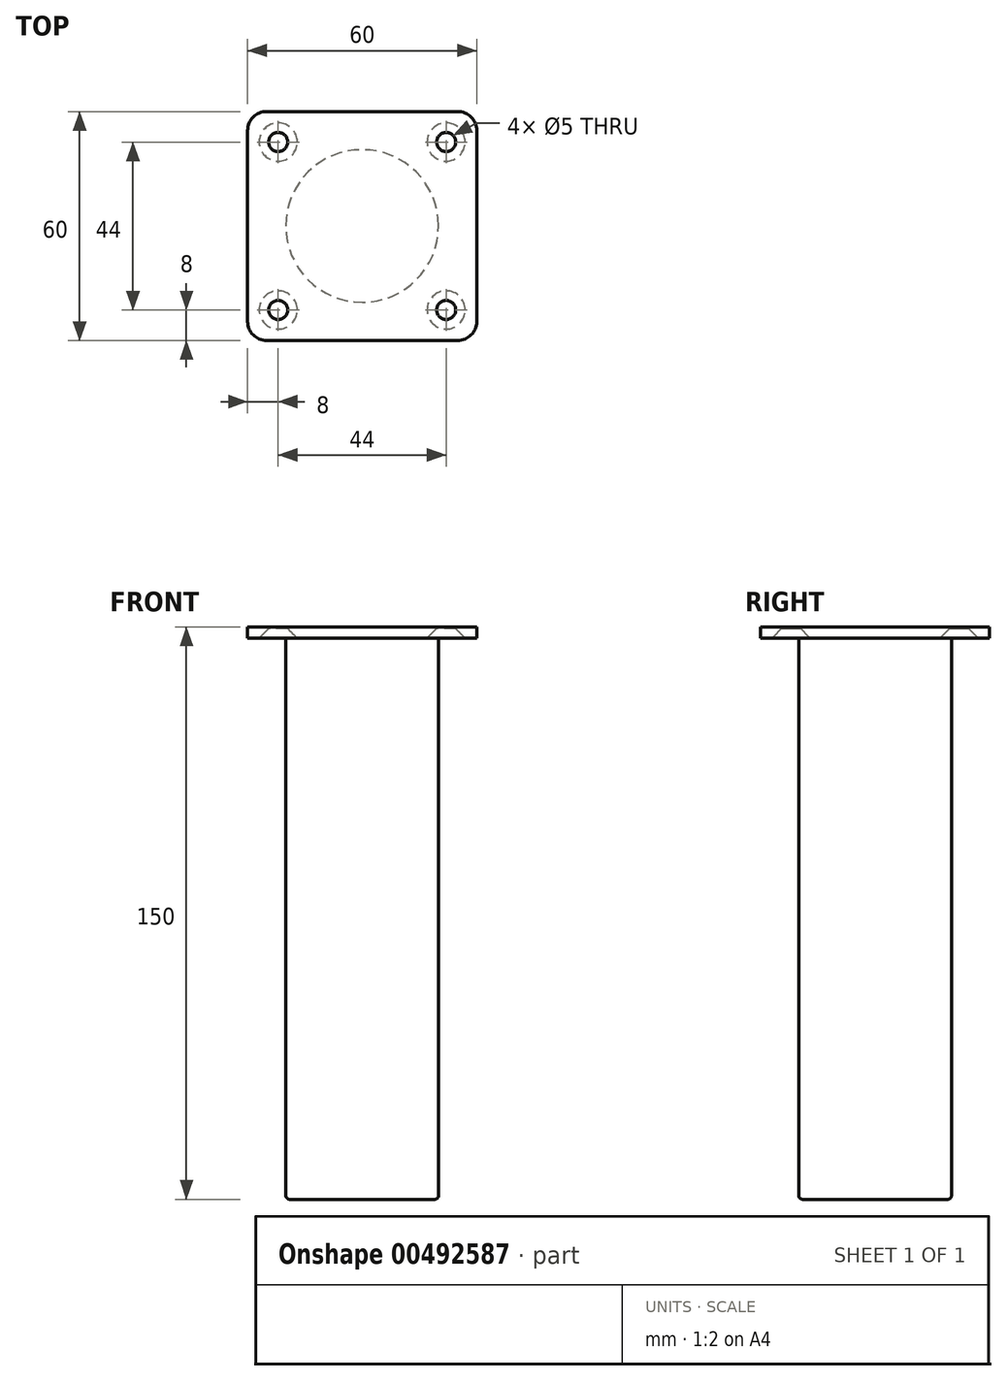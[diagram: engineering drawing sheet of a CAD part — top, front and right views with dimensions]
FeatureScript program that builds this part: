
annotation { "Feature Type Name" : "Feature", "Feature Type Description" : "" }
export const myFeature = defineFeature(function(context is Context, id is Id, definition is map)
    precondition{}
    {
        {
            var Q0;
            Q0=qCreatedBy(makeId("Top.planeOp"),FACE);
            var sketch = newSketch(context, id + "F0", { "sketchPlane" : qUnion([Q0])});
            skLineSegment(sketch, "E0.bottom", {"start": v(-30, 30) * mm, "end": v(30, 30) * mm});
            skLineSegment(sketch, "E0.top", {"start": v(-30, -30) * mm, "end": v(30, -30) * mm});
            skLineSegment(sketch, "E0.left", {"start": v(-30, 30) * mm, "end": v(-30, -30) * mm});
            skLineSegment(sketch, "E0.right", {"start": v(30, 30) * mm, "end": v(30, -30) * mm});
            skPoint(sketch, "E0.middle", {"position": v(0, 0) * mm});
            skSolve(sketch);
        }
        {
            var Q0;
            Q0=makeQuery(id+"F0.imprint","IMPRINT",FACE,{"disambiguationData":[TD([[makeQuery(id+"F0.imprint","IMPRINT",EDGE,{"derivedFrom":sQuery(id+"F0.wireOp",EDGE,"E0.bottom")}),-1.0]])]});
            extrude(context, id + "F1", {"entities" : qUnion([Q0]), "oppositeDirection" : true, "depth" : 3 * mm});
        }
        {
            var Q0;
            Q0=makeQuery(id+"F1.opExtrude","CAP_FACE",FACE,{"disambiguationData":[OSD([sQuery(id+"F0.wireOp",EDGE,"E0.bottom"),sQuery(id+"F0.wireOp",EDGE,"E0.top"),sQuery(id+"F0.wireOp",EDGE,"E0.left"),sQuery(id+"F0.wireOp",EDGE,"E0.right")])],"isStart":false});
            var sketch = newSketch(context, id + "F2", { "sketchPlane" : qUnion([Q0])});
            skCircle(sketch, "E1", {"center": v(0, 0) * mm, "radius": 20 * mm});
            skSolve(sketch);
        }
        {
            var Q0;
            Q0 = qSketchRegion(id + "F2", true);
            extrude(context, id + "F3", {"entities" : qUnion([Q0]), "operationType" : NewBodyOperationType.ADD, "depth" : 147 * mm});
        }
        {
            var Q0;
            Q0=makeQuery(id+"F1.opExtrude","SWEPT_EDGE",EDGE,{"disambiguationData":[OSD([sQuery(id+"F0.wireOp",EDGE,"E0.top"),sQuery(id+"F0.wireOp",EDGE,"E0.left")])]});
            var Q1;
            Q1=makeQuery(id+"F1.opExtrude","SWEPT_EDGE",EDGE,{"disambiguationData":[OSD([sQuery(id+"F0.wireOp",EDGE,"E0.top"),sQuery(id+"F0.wireOp",EDGE,"E0.right")])]});
            var Q2;
            Q2=makeQuery(id+"F1.opExtrude","SWEPT_EDGE",EDGE,{"disambiguationData":[OSD([sQuery(id+"F0.wireOp",EDGE,"E0.bottom"),sQuery(id+"F0.wireOp",EDGE,"E0.right")])]});
            var Q3;
            Q3=makeQuery(id+"F1.opExtrude","SWEPT_EDGE",EDGE,{"disambiguationData":[OSD([sQuery(id+"F0.wireOp",EDGE,"E0.bottom"),sQuery(id+"F0.wireOp",EDGE,"E0.left")])]});
            fillet(context, id + "F4", {"entities" : qUnion([Q0, Q1, Q2, Q3]), "radius" : 5 * mm, "tangentPropagation" : true, "allowEdgeOverflow" : false});
        }
        {
            var Q0;
            Q0=makeQuery(id+"F1.opExtrude","CAP_FACE",FACE,{"disambiguationData":[OSD([sQuery(id+"F0.wireOp",EDGE,"E0.bottom"),sQuery(id+"F0.wireOp",EDGE,"E0.top"),sQuery(id+"F0.wireOp",EDGE,"E0.left"),sQuery(id+"F0.wireOp",EDGE,"E0.right")])],"isStart":false});
            var sketch = newSketch(context, id + "F5", { "sketchPlane" : qUnion([Q0])});
            skPoint(sketch, "E2", {"position": v(-22, 22) * mm});
            skPoint(sketch, "E3.0.1.0", {"position": v(-22, -22) * mm});
            skPoint(sketch, "E3.1.0.0", {"position": v(22, 22) * mm});
            skPoint(sketch, "E3.1.1.0", {"position": v(22, -22) * mm});
            skLineSegment(sketch, "E3.direction1", {"start": v(-22, 22) * mm, "end": v(22, 22) * mm, "construction": true});
            skLineSegment(sketch, "E3.direction2", {"start": v(-22, 22) * mm, "end": v(-22, -22) * mm, "construction": true});
            skSolve(sketch);
        }
        {
            var Q0;
            Q0=sQuery(id+"F5.wireOp",VERTEX,"E2");
            var Q1;
            Q1=sQuery(id+"F5.wireOp",VERTEX,"E3.1.0.0");
            var Q2;
            Q2=sQuery(id+"F5.wireOp",VERTEX,"E3.1.1.0");
            var Q3;
            Q3=sQuery(id+"F5.wireOp",VERTEX,"E3.0.1.0");
            var Q4;
            Q4=makeQuery(id+"F1.opExtrude","SWEPT_BODY",BODY,{"disambiguationData":[OSD([sQuery(id+"F0.wireOp",EDGE,"E0.bottom"),sQuery(id+"F0.wireOp",EDGE,"E0.top"),sQuery(id+"F0.wireOp",EDGE,"E0.left"),sQuery(id+"F0.wireOp",EDGE,"E0.right")])]});
            hole(context, id + "F6", {"style" : HoleStyle.C_SINK, "endStyle" : HoleEndStyle.THROUGH, "holeDiameter" : 5 * mm, "cSinkDiameter" : 10 * mm, "cSinkAngle" : 90 * degree, "isTappedThrough" : true, "tappedDepth" : 12 * mm, "tapClearance" : 3, "locations" : qUnion([Q0, Q1, Q2, Q3]), "scope" : qUnion([Q4])});
        }
        {
            var Q0;
            Q0=makeQuery(id+"F3.opExtrude","CAP_EDGE",EDGE,{"disambiguationData":[OSD([sQuery(id+"F2.wireOp",EDGE,"E1")])],"isStart":false});
            fillet(context, id + "F7", {"entities" : qUnion([Q0]), "radius" : 1 * mm, "tangentPropagation" : true, "allowEdgeOverflow" : false});
        }
    });
